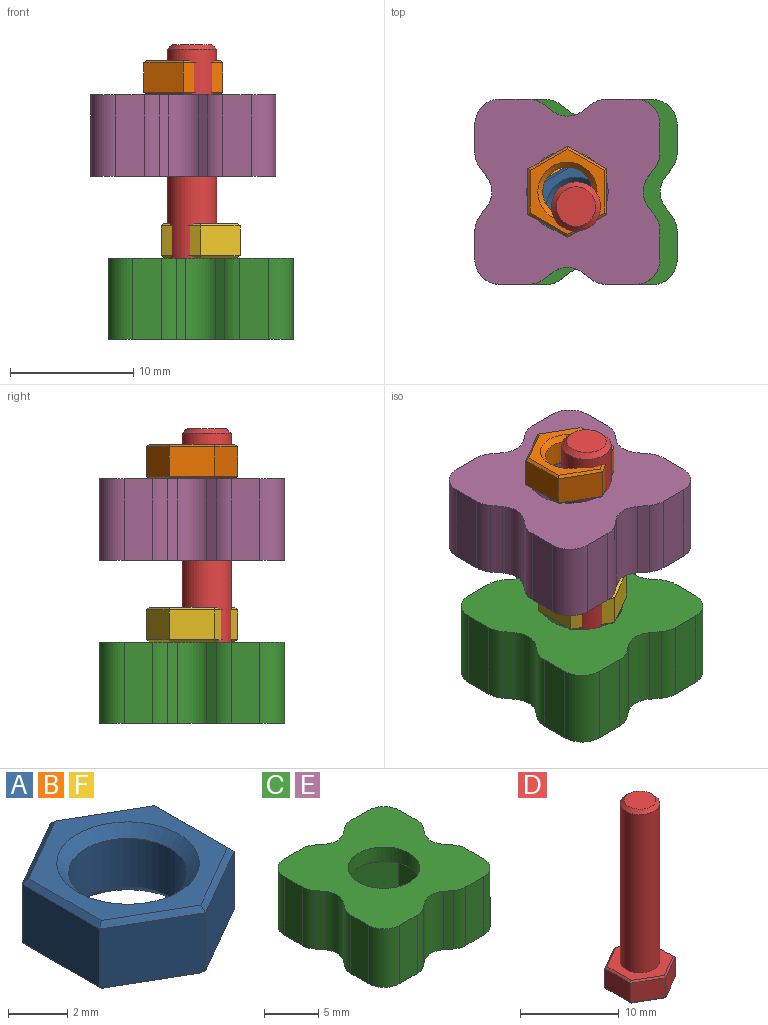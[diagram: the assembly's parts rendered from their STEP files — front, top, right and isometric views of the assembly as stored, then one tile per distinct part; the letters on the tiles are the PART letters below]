
ASSEMBLY  parts=6 mates=5
PART A: 23 faces, bbox 6.4x7.4x2.8 mm
  f0: plane 3.2x2.4mm, normal (-0.5,-0.87,0), area 8.9mm2, adj f1,f6,f10,f16
  f1: plane 3.2x2.4mm, normal (0.5,-0.87,0), area 8.9mm2, adj f0,f2,f12,f18
  f2: plane 3.7x2.4mm, normal (1,0,0), area 8.9mm2, adj f1,f3,f14,f20
  f3: plane 3.2x2.4mm, normal (0.5,0.87,0), area 8.9mm2, adj f2,f4,f13,f19
  f4: plane 3.2x2.4mm, normal (-0.5,0.87,0), area 8.9mm2, adj f3,f6,f11,f17
  f5: cylinder r=2mm len=4mm, axis (0,0,-1), area 25.1mm2, adj f21,f22
  f6: plane 3.7x2.4mm, normal (-1,0,0), area 8.9mm2, adj f0,f4,f9,f15
  f7: plane 6.93x6mm, normal (0,0,1), area 13.1mm2, adj f15,f16,f17,f18,f19,f20,f21
  f8: plane 6.93x6mm, normal (0,0,-1), area 13.1mm2, adj f9,f10,f11,f12,f13,f14,f22
  f9: plane 3.7x0.2mm, normal (-0.71,0,-0.71), area 1mm2, adj f6,f8,f10,f11
  f10: plane 3.2x1.96mm, normal (-0.35,-0.61,-0.71), area 1mm2, adj f0,f8,f9,f12
  f11: plane 3.2x1.96mm, normal (-0.35,0.61,-0.71), area 1mm2, adj f4,f8,f9,f13
  f12: plane 3.2x1.96mm, normal (0.35,-0.61,-0.71), area 1mm2, adj f1,f8,f10,f14
  f13: plane 3.2x1.96mm, normal (0.35,0.61,-0.71), area 1mm2, adj f3,f8,f11,f14
  f14: plane 3.7x0.2mm, normal (0.71,0,-0.71), area 1mm2, adj f2,f8,f12,f13
  f15: plane 3.7x0.2mm, normal (-0.71,0,0.71), area 1mm2, adj f6,f7,f16,f17
  f16: plane 3.2x1.96mm, normal (-0.35,-0.61,0.71), area 1mm2, adj f0,f7,f15,f18
  f17: plane 3.2x1.96mm, normal (-0.35,0.61,0.71), area 1mm2, adj f4,f7,f15,f19
  f18: plane 3.2x1.96mm, normal (0.35,-0.61,0.71), area 1mm2, adj f1,f7,f16,f20
  f19: plane 3.2x1.96mm, normal (0.35,0.61,0.71), area 1mm2, adj f3,f7,f17,f20
  f20: plane 3.7x0.2mm, normal (0.71,0,0.71), area 1mm2, adj f2,f7,f18,f19
  f21: cone r=2mm half-angle=45deg, axis (0,0,1), area 7.8mm2, adj f5,f7
  f22: cone r=2.4mm half-angle=45deg, axis (0,0,-1), area 7.8mm2, adj f5,f8
PART B: same geometry as A
PART C: 49 faces, bbox 15x15x6.6 mm
  f0: plane 6.6x0.77mm, normal (-0.6,0.8,0), area 6.3mm2, adj f16,f17,f26,f41
  f1: plane 6.6x0.77mm, normal (0.6,0.8,0), area 6.3mm2, adj f16,f17,f26,f27
  f2: plane 6.6x2.33mm, normal (0,1,0), area 15.4mm2, adj f16,f17,f27,f28
  f3: plane 6.6x2.33mm, normal (-1,0,0), area 15.4mm2, adj f16,f17,f28,f29
  f4: plane 6.6x0.77mm, normal (-0.8,-0.6,0), area 6.3mm2, adj f16,f17,f29,f30
  f5: plane 6.6x0.77mm, normal (-0.8,0.6,0), area 6.3mm2, adj f16,f17,f30,f31
  f6: plane 6.6x2.33mm, normal (-1,0,0), area 15.4mm2, adj f16,f17,f31,f32
  f7: plane 6.6x2.33mm, normal (0,-1,0), area 15.4mm2, adj f16,f17,f32,f33
  f8: plane 6.6x0.77mm, normal (0.6,-0.8,0), area 6.3mm2, adj f16,f17,f33,f34
  f9: plane 6.6x0.77mm, normal (-0.6,-0.8,0), area 6.3mm2, adj f16,f17,f34,f35
  f10: plane 6.6x2.33mm, normal (0,-1,0), area 15.4mm2, adj f16,f17,f35,f36
  f11: plane 6.6x2.33mm, normal (1,0,0), area 15.4mm2, adj f16,f17,f36,f37
  f12: plane 6.6x0.77mm, normal (0.8,0.6,0), area 6.3mm2, adj f16,f17,f37,f38
  f13: plane 6.6x0.77mm, normal (0.8,-0.6,0), area 6.3mm2, adj f16,f17,f38,f39
  f14: plane 6.6x2.33mm, normal (1,0,0), area 15.4mm2, adj f16,f17,f39,f40
  f15: plane 6.6x2.33mm, normal (0,1,0), area 15.4mm2, adj f16,f17,f40,f41
  f16: plane 15x15mm, normal (0,0,1), area 169.9mm2, adj f0,f1,f2,f3,f4,f5,f6,f7
  f17: plane 15x15mm, normal (0,0,-1), area 124.7mm2, adj f0,f1,f2,f3,f4,f5,f6,f7
  f18: cylinder r=3.3mm len=6.6mm, axis (0,0,1), area 33.2mm2, adj f16,f48
  f19: plane 10.6x9.18mm, normal (0,0,-1), area 34.5mm2, adj f20,f21,f22,f23,f24,f25,f48
  f20: plane 4.6x4.59mm, normal (-0.5,-0.87,0), area 24.4mm2, adj f19,f21,f25,f44
  f21: plane 4.6x4.59mm, normal (0.5,-0.87,0), area 24.4mm2, adj f19,f20,f22,f46
  f22: plane 5.3x4.6mm, normal (1,0,0), area 24.4mm2, adj f19,f21,f23,f47
  f23: plane 4.6x4.59mm, normal (0.5,0.87,0), area 24.4mm2, adj f19,f22,f24,f45
  f24: plane 4.6x4.59mm, normal (-0.5,0.87,0), area 24.4mm2, adj f19,f23,f25,f43
  f25: plane 5.3x4.6mm, normal (-1,0,0), area 24.4mm2, adj f19,f20,f24,f42
  f26: cylinder r=2mm len=6.6mm, axis (0,0,-1), area 17mm2, adj f0,f1,f16,f17
  f27: cylinder r=2mm len=6.6mm, axis (0,0,1), area 8.5mm2, adj f1,f2,f16,f17
  f28: cylinder r=2mm len=6.6mm, axis (0,0,1), area 20.7mm2, adj f2,f3,f16,f17
  f29: cylinder r=2mm len=6.6mm, axis (0,0,-1), area 8.5mm2, adj f3,f4,f16,f17
  f30: cylinder r=2mm len=6.6mm, axis (0,0,-1), area 17mm2, adj f4,f5,f16,f17
  f31: cylinder r=2mm len=6.6mm, axis (0,0,-1), area 8.5mm2, adj f5,f6,f16,f17
  f32: cylinder r=2mm len=6.6mm, axis (0,0,1), area 20.7mm2, adj f6,f7,f16,f17
  f33: cylinder r=2mm len=6.6mm, axis (0,0,1), area 8.5mm2, adj f7,f8,f16,f17
  f34: cylinder r=2mm len=6.6mm, axis (0,0,-1), area 17mm2, adj f8,f9,f16,f17
  f35: cylinder r=2mm len=6.6mm, axis (0,0,1), area 8.5mm2, adj f9,f10,f16,f17
  f36: cylinder r=2mm len=6.6mm, axis (0,0,1), area 20.7mm2, adj f10,f11,f16,f17
  f37: cylinder r=2mm len=6.6mm, axis (0,0,-1), area 8.5mm2, adj f11,f12,f16,f17
  f38: cylinder r=2mm len=6.6mm, axis (0,0,-1), area 17mm2, adj f12,f13,f16,f17
  f39: cylinder r=2mm len=6.6mm, axis (0,0,-1), area 8.5mm2, adj f13,f14,f16,f17
  f40: cylinder r=2mm len=6.6mm, axis (0,0,1), area 20.7mm2, adj f14,f15,f16,f17
  f41: cylinder r=2mm len=6.6mm, axis (0,0,1), area 8.5mm2, adj f0,f15,f16,f17
  f42: plane 5.53x0.2mm, normal (-0.71,0,-0.71), area 1.5mm2, adj f17,f25,f43,f44
  f43: plane 4.79x2.88mm, normal (-0.35,0.61,-0.71), area 1.5mm2, adj f17,f24,f42,f45
  f44: plane 4.79x2.88mm, normal (-0.35,-0.61,-0.71), area 1.5mm2, adj f17,f20,f42,f46
  f45: plane 4.79x2.88mm, normal (0.35,0.61,-0.71), area 1.5mm2, adj f17,f23,f43,f47
  f46: plane 4.79x2.88mm, normal (0.35,-0.61,-0.71), area 1.5mm2, adj f17,f21,f44,f47
  f47: plane 5.53x0.2mm, normal (0.71,0,-0.71), area 1.5mm2, adj f17,f22,f45,f46
  f48: cone r=3.3mm half-angle=45deg, axis (0,0,-1), area 6mm2, adj f18,f19
PART D: 23 faces, bbox 6.4x7.4x22.8 mm
  f0: plane 3.7x2.4mm, normal (1,0,0), area 8.9mm2, adj f1,f5,f15,f21
  f1: plane 3.2x2.4mm, normal (0.5,0.87,0), area 8.9mm2, adj f0,f2,f13,f19
  f2: plane 3.2x2.4mm, normal (-0.5,0.87,0), area 8.9mm2, adj f1,f3,f11,f17
  f3: plane 3.7x2.4mm, normal (-1,0,0), area 8.9mm2, adj f2,f4,f10,f16
  f4: plane 3.2x2.4mm, normal (-0.5,-0.87,0), area 8.9mm2, adj f3,f5,f12,f18
  f5: plane 3.2x2.4mm, normal (0.5,-0.87,0), area 8.9mm2, adj f0,f4,f14,f20
  f6: plane 6.93x6mm, normal (0,0,1), area 18.6mm2, adj f8,f10,f11,f12,f13,f14,f15
  f7: plane 6.93x6mm, normal (0,0,-1), area 31.2mm2, adj f16,f17,f18,f19,f20,f21
  f8: cylinder r=2mm len=19.6mm, axis (0,0,-1), area 246.3mm2, adj f6,f22
  f9: plane 3.2x3.2mm, normal (0,0,1), area 8mm2, adj f22
  f10: plane 3.7x0.2mm, normal (-0.71,0,0.71), area 1mm2, adj f3,f6,f11,f12
  f11: plane 3.2x1.96mm, normal (-0.35,0.61,0.71), area 1mm2, adj f2,f6,f10,f13
  f12: plane 3.2x1.96mm, normal (-0.35,-0.61,0.71), area 1mm2, adj f4,f6,f10,f14
  f13: plane 3.2x1.96mm, normal (0.35,0.61,0.71), area 1mm2, adj f1,f6,f11,f15
  f14: plane 3.2x1.96mm, normal (0.35,-0.61,0.71), area 1mm2, adj f5,f6,f12,f15
  f15: plane 3.7x0.2mm, normal (0.71,0,0.71), area 1mm2, adj f0,f6,f13,f14
  f16: plane 3.7x0.2mm, normal (-0.71,0,-0.71), area 1mm2, adj f3,f7,f17,f18
  f17: plane 3.2x1.96mm, normal (-0.35,0.61,-0.71), area 1mm2, adj f2,f7,f16,f19
  f18: plane 3.2x1.96mm, normal (-0.35,-0.61,-0.71), area 1mm2, adj f4,f7,f16,f20
  f19: plane 3.2x1.96mm, normal (0.35,0.61,-0.71), area 1mm2, adj f1,f7,f17,f21
  f20: plane 3.2x1.96mm, normal (0.35,-0.61,-0.71), area 1mm2, adj f5,f7,f18,f21
  f21: plane 3.7x0.2mm, normal (0.71,0,-0.71), area 1mm2, adj f0,f7,f19,f20
  f22: cone r=1.6mm half-angle=45deg, axis (0,0,-1), area 6.4mm2, adj f8,f9
PART E: same geometry as C
PART F: same geometry as A
PLACE A rot(axis=(1,0,0),180deg) t=(-0.69,-1.2,47.12)mm
PLACE B rot(axis=(1,0,0),180deg) t=(-1.39,0,52.62)mm
PLACE C at identity fixed
PLACE D rot(axis=(0,0,1),0deg) t=(-0.69,-1.2,1.1)mm
PLACE E rot(axis=(0,0,-1),0deg) t=(-1.39,0,13.22)mm
PLACE F rot(axis=(0,0,1),0deg) t=(0,0,-23.4)mm
MATE fastened D.f4 <-> C.f23  axis (-0.5,-0.87,0) through (-2.29,-3.98,2.5)mm
MATE fastened A.f3 <-> E.f24  axis (0.5,-0.87,0) through (0.91,-3.97,15.72)mm
MATE slider A.f5 <-> D.f8  axis (0,0,1) through (-0.69,-1.2,15.72)mm
MATE fastened C.f18 <-> F.f5  axis (0,0,1) through (0,0,6.6)mm
MATE fastened B.f5 <-> E.f18  axis (0,0,-1) through (-1.39,0,19.82)mm
